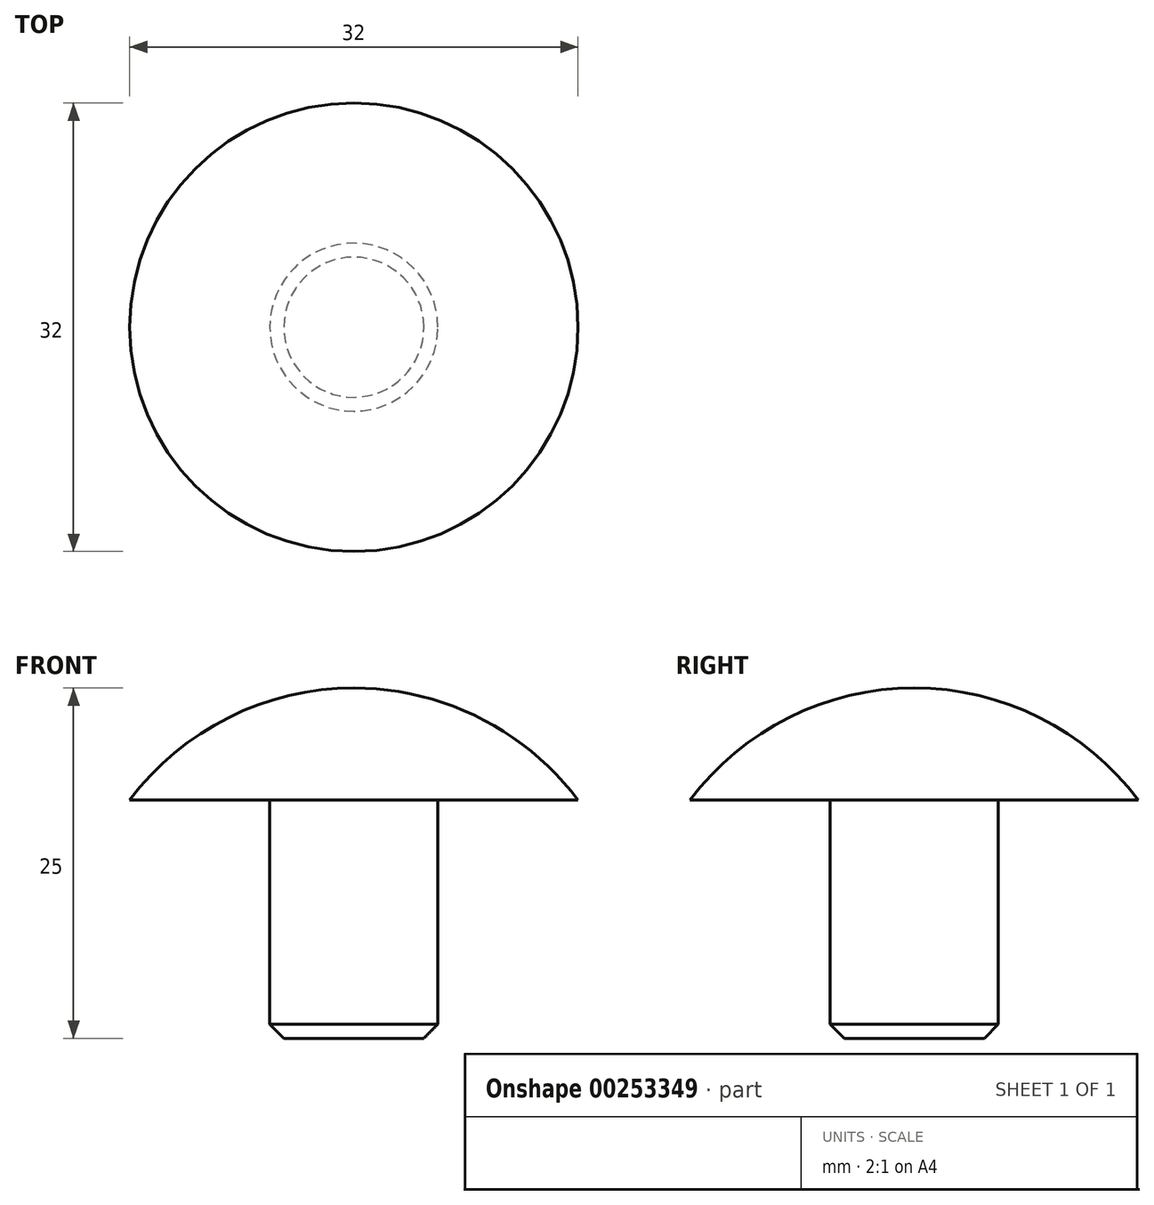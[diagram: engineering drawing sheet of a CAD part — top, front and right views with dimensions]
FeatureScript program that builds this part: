
annotation { "Feature Type Name" : "Feature", "Feature Type Description" : "" }
export const myFeature = defineFeature(function(context is Context, id is Id, definition is map)
    precondition{}
    {
        {
            var Q0;
            Q0=qCreatedBy(makeId("Front.planeOp"),FACE);
            var sketch = newSketch(context, id + "F0", { "sketchPlane" : qUnion([Q0])});
            skLineSegment(sketch, "E0", {"start": v(0, -17) * mm, "end": v(6, -17) * mm});
            skLineSegment(sketch, "E1", {"start": v(6, -17) * mm, "end": v(6, 0) * mm});
            skLineSegment(sketch, "E2", {"start": v(6, 0) * mm, "end": v(16, 0) * mm});
            skArc(sketch, "E3", {"start": v(16, 0) * mm, "mid": v(8.94, 5.89) * mm, "end": v(0, 8) * mm});
            skLineSegment(sketch, "E4", {"start": v(0, 8) * mm, "end": v(0, -17) * mm});
            skLineSegment(sketch, "E5", {"start": v(0, 8) * mm, "end": v(-15.85, 8) * mm, "construction": true});
            skSolve(sketch);
        }
        {
            var Q0;
            Q0 = qSketchRegion(id + "F0", true);
            var Q1;
            Q1=sQuery(id+"F0.wireOp",EDGE,"E4");
            revolve(context, id + "F1", {"entities" : qUnion([Q0]), "axis" : qUnion([Q1]), "revolveType" : RevolveType.FULL});
        }
        {
            var Q0;
            Q0=makeQuery(id+"F1.opRevolve","SWEPT_EDGE",EDGE,{"disambiguationData":[OSD([sQuery(id+"F0.wireOp",EDGE,"E0"),sQuery(id+"F0.wireOp",EDGE,"E1")])]});
            chamfer(context, id + "F2", {"entities" : qUnion([Q0]), "width" : 1 * mm, "tangentPropagation" : true});
        }
    });
